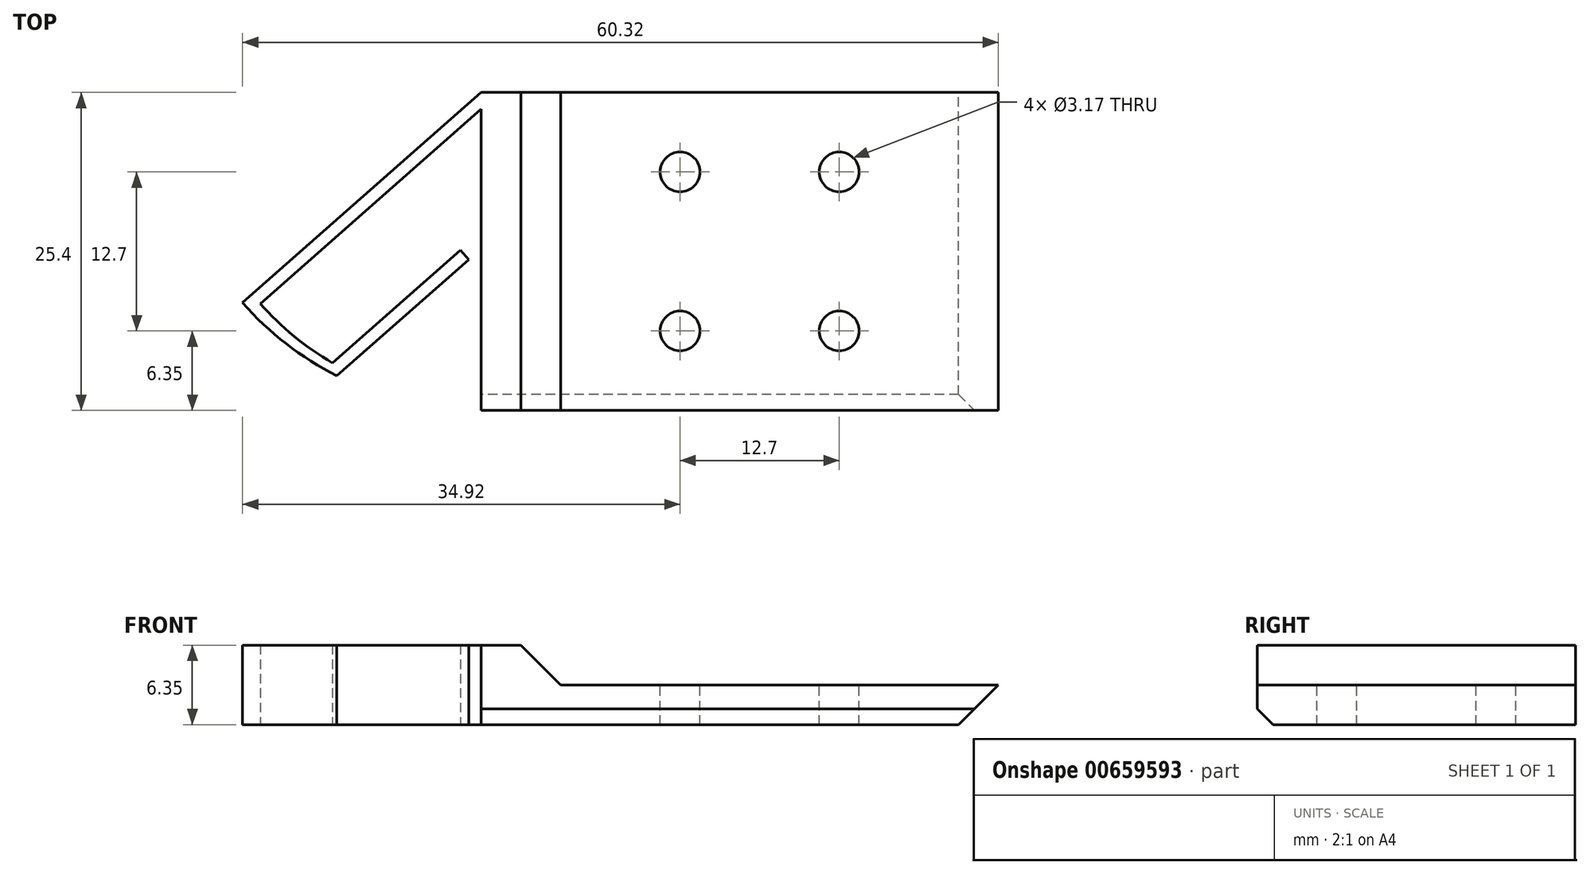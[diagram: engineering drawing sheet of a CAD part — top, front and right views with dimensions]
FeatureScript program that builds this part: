
annotation { "Feature Type Name" : "Feature", "Feature Type Description" : "" }
export const myFeature = defineFeature(function(context is Context, id is Id, definition is map)
    precondition{}
    {
        {
            var Q0;
            Q0=qCreatedBy(makeId("Top.planeOp"),FACE);
            var sketch = newSketch(context, id + "F0", { "sketchPlane" : qUnion([Q0])});
            skLineSegment(sketch, "E0.bottom", {"start": v(28.58, -12.7) * mm, "end": v(-28.58, -12.7) * mm});
            skLineSegment(sketch, "E0.top", {"start": v(28.58, 12.7) * mm, "end": v(-28.58, 12.7) * mm});
            skLineSegment(sketch, "E0.left", {"start": v(28.58, -12.7) * mm, "end": v(28.58, 12.7) * mm});
            skLineSegment(sketch, "E0.right", {"start": v(-28.57, -12.7) * mm, "end": v(-28.57, 12.7) * mm});
            skPoint(sketch, "E0.middle", {"position": v(0, 0) * mm});
            skLineSegment(sketch, "E1", {"start": v(-9.53, 11.37) * mm, "end": v(-9.52, -12.7) * mm});
            skLineSegment(sketch, "E2", {"start": v(0, -12.7) * mm, "end": v(0, 12.7) * mm});
            skPoint(sketch, "E3", {"position": v(-22.22, -12.7) * mm});
            skLineSegment(sketch, "E4", {"start": v(-9.53, 12.7) * mm, "end": v(-28.57, -4.1) * mm});
            skPoint(sketch, "E5", {"position": v(-19.05, -12.7) * mm});
            skArc(sketch, "E6", {"start": v(-28.57, -4.1) * mm, "mid": v(-25.09, -7.37) * mm, "end": v(-21.05, -9.94) * mm});
            skLineSegment(sketch, "E7", {"start": v(-21.05, -9.94) * mm, "end": v(-10.53, -0.66) * mm});
            skLineSegment(sketch, "E8", {"start": v(-10.53, -0.66) * mm, "end": v(-11.19, 0.1) * mm});
            skLineSegment(sketch, "E9", {"start": v(-11.19, 0.1) * mm, "end": v(-11.19, 0.1) * mm});
            skLineSegment(sketch, "E10", {"start": v(-9.53, 11.37) * mm, "end": v(-27.15, -4.18) * mm});
            skArc(sketch, "E11", {"start": v(-27.15, -4.18) * mm, "mid": v(-24.46, -6.77) * mm, "end": v(-21.4, -8.91) * mm});
            skLineSegment(sketch, "E12", {"start": v(-21.4, -8.91) * mm, "end": v(-11.19, 0.1) * mm});
            skSolve(sketch);
        }
        {
            var Q0;
            {var subQ0=sQuery(id+"F0.wireOp",EDGE,"E0.left");Q0=makeQuery(id+"F0.imprint","IMPRINT",FACE,{"disambiguationData":[TD([[makeQuery(id+"F0.imprint","IMPRINT",EDGE,{"derivedFrom":subQ0}),1.0]])]});}
            var Q1;
            {var subQ1=sQuery(id+"F0.wireOp",EDGE,"E1");Q1=makeQuery(id+"F0.imprint","IMPRINT",FACE,{"disambiguationData":[TD([[makeQuery(id+"F0.imprint","IMPRINT",EDGE,{"derivedFrom":subQ1}),1.0]])]});}
            var Q2;
            {var subQ0=sQuery(id+"F0.wireOp",EDGE,"Ll8NUgnO-918t-zldm-zNWz-RsUZQomu35K8");Q2=makeQuery(id+"F0.imprint","IMPRINT",FACE,{"disambiguationData":[TD([[makeQuery(id+"F0.imprint","IMPRINT",EDGE,{"derivedFrom":subQ0}),1.0]])]});}
            extrude(context, id + "F1", {"entities" : qUnion([Q0, Q1, Q2]), "depth" : 3.17 * mm, "offsetDistance" : 25.4 * mm});
        }
        {
            var Q0;
            {var subQ1=sQuery(id+"F0.wireOp",EDGE,"E1");Q0=makeQuery(id+"F0.imprint","IMPRINT",FACE,{"disambiguationData":[TD([[makeQuery(id+"F0.imprint","IMPRINT",EDGE,{"derivedFrom":subQ1}),1.0]])]});}
            extrude(context, id + "F2", {"entities" : qUnion([Q0]), "operationType" : NewBodyOperationType.ADD, "depth" : 6.35 * mm, "offsetDistance" : 25.4 * mm});
        }
        {
            var Q0;
            Q0=makeQuery(id+"F2.opExtrude","CAP_EDGE",EDGE,{"disambiguationData":[OSD([sQuery(id+"F0.wireOp",EDGE,"E2")])],"isStart":false});
            chamfer(context, id + "F3", {"entities" : qUnion([Q0]), "width" : 6.35 * mm, "tangentPropagation" : true});
        }
        {
            var Q0;
            {var subQ0=sQuery(id+"F0.wireOp",EDGE,"E0.left");Q0=makeQuery(id+"F37SAEC6IVc2ddh_1.boolean.opBoolean","MERGE",FACE,{"derivedFrom":[makeQuery(id+"F1.opExtrude","SWEPT_FACE",FACE,{"disambiguationData":[OSD([subQ0])]}),makeQuery(id+"F37SAEC6IVc2ddh_1.opExtrude","SWEPT_FACE",FACE,{"disambiguationData":[OSD([subQ0])]})]});}
            cPlane(context, id + "F4", {"entities" : qUnion([Q0]), "cplaneType" : CPlaneType.OFFSET, "offset" : 3.17 * mm, "width" : 152.4 * mm, "height" : 152.4 * mm});
        }
        {
            var Q0;
            {var subQ0=sQuery(id+"F0.wireOp",EDGE,"E1");Q0=makeQuery(id+"F2.boolean.opBoolean","MERGE",FACE,{"derivedFrom":[makeQuery(id+"F1.opExtrude","SWEPT_FACE",FACE,{"disambiguationData":[OSD([subQ0])]}),makeQuery(id+"F2.opExtrude","SWEPT_FACE",FACE,{"disambiguationData":[OSD([subQ0])]})]});}
            var sketch = newSketch(context, id + "F5", { "sketchPlane" : qUnion([Q0])});
            skLineSegment(sketch, "E13", {"start": v(12.7, 0) * mm, "end": v(12.7, 1.27) * mm});
            skLineSegment(sketch, "E14", {"start": v(12.7, 1.27) * mm, "end": v(11.43, 0) * mm});
            skLineSegment(sketch, "E15", {"start": v(11.43, 0) * mm, "end": v(12.7, 0) * mm});
            skSolve(sketch);
        }
        {
            var Q0;
            {var subQ0=sQuery(id+"F0.wireOp",EDGE,"E0.top");Q0=makeQuery(id+"F2.boolean.opBoolean","MERGE",FACE,{"derivedFrom":[makeQuery(id+"F1.opExtrude","SWEPT_FACE",FACE,{"disambiguationData":[OSD([subQ0])]}),makeQuery(id+"F2.opExtrude","SWEPT_FACE",FACE,{"disambiguationData":[OSD([subQ0])]})]});}
            var sketch = newSketch(context, id + "F6", { "sketchPlane" : qUnion([Q0])});
            skLineSegment(sketch, "E16", {"start": v(-28.58, 3.18) * mm, "end": v(-31.75, 3.18) * mm});
            skLineSegment(sketch, "E17", {"start": v(-31.75, 3.18) * mm, "end": v(-28.58, 0) * mm});
            skLineSegment(sketch, "E18", {"start": v(-28.58, 0) * mm, "end": v(-28.58, 3.18) * mm});
            skSolve(sketch);
        }
        {
            var Q0;
            Q0=makeQuery(id+"F6.imprint","IMPRINT",FACE,{"disambiguationData":[TD([[makeQuery(id+"F6.imprint","IMPRINT",EDGE,{"derivedFrom":sQuery(id+"F6.wireOp",EDGE,"E18")}),1.0]])]});
            var Q1;
            Q1=makeQuery(id+"F6.imprint","IMPRINT",FACE,{"disambiguationData":[TD([[makeQuery(id+"F6.imprint","IMPRINT",EDGE,{"derivedFrom":sQuery(id+"F6.wireOp",EDGE,"E16")}),1.0]])]});
            extrude(context, id + "F7", {"entities" : qUnion([Q0, Q1]), "operationType" : NewBodyOperationType.ADD, "oppositeDirection" : true, "depth" : 25.4 * mm, "offsetDistance" : 25.4 * mm});
        }
        {
            var Q0;
            Q0=makeQuery(id+"F5.imprint","IMPRINT",FACE,{"disambiguationData":[TD([[makeQuery(id+"F5.imprint","IMPRINT",EDGE,{"derivedFrom":sQuery(id+"F5.wireOp",EDGE,"E13")}),-1.0]])]});
            extrude(context, id + "F8", {"entities" : qUnion([Q0]), "operationType" : NewBodyOperationType.REMOVE, "oppositeDirection" : true, "depth" : 50.8 * mm, "offsetDistance" : 25.4 * mm});
        }
        {
            var Q0;
            Q0=makeQuery(id+"F1.opExtrude","SWEPT_BODY",BODY,{"disambiguationData":[OSD([sQuery(id+"F0.wireOp",EDGE,"E0.bottom"),sQuery(id+"F0.wireOp",EDGE,"E0.top"),sQuery(id+"F0.wireOp",EDGE,"E0.left"),sQuery(id+"F0.wireOp",EDGE,"E1"),sQuery(id+"F0.wireOp",EDGE,"E4"),sQuery(id+"F0.wireOp",EDGE,"E6"),sQuery(id+"F0.wireOp",EDGE,"E7"),sQuery(id+"F0.wireOp",EDGE,"E8"),sQuery(id+"F0.wireOp",EDGE,"E10"),sQuery(id+"F0.wireOp",EDGE,"E11"),sQuery(id+"F0.wireOp",EDGE,"E12")])]});
            var Q1;
            Q1=qCreatedBy(id+"F4.planeOp",FACE);
            mirror(context, id + "F9", {"entities" : qUnion([Q0]), "mirrorPlane" : qUnion([Q1])});
        }
        {
            var Q0;
            {var subQ0=sQuery(id+"F0.wireOp",EDGE,"E0.top");Q0=makeQuery(id+"F7.boolean.opBoolean","MERGE",FACE,{"derivedFrom":[makeQuery(id+"F1.opExtrude","CAP_FACE",FACE,{"disambiguationData":[OSD([sQuery(id+"F0.wireOp",EDGE,"E0.bottom"),subQ0,sQuery(id+"F0.wireOp",EDGE,"E0.left"),sQuery(id+"F0.wireOp",EDGE,"E1"),sQuery(id+"F0.wireOp",EDGE,"E4"),sQuery(id+"F0.wireOp",EDGE,"E6"),sQuery(id+"F0.wireOp",EDGE,"E7"),sQuery(id+"F0.wireOp",EDGE,"E8"),sQuery(id+"F0.wireOp",EDGE,"E10"),sQuery(id+"F0.wireOp",EDGE,"E11"),sQuery(id+"F0.wireOp",EDGE,"E12")])],"isStart":false}),makeQuery(id+"F7.opExtrude","SWEPT_FACE",FACE,{"disambiguationData":[OSD([subQ0,sQuery(id+"F6.wireOp",EDGE,"E16")])]})]});}
            var sketch = newSketch(context, id + "F10", { "sketchPlane" : qUnion([Q0])});
            skLineSegment(sketch, "E19", {"start": v(31.75, 0) * mm, "end": v(19.05, 0) * mm, "construction": true});
            skPoint(sketch, "E19.endSnap0", {"position": v(-3.17, 0) * mm});
            skLineSegment(sketch, "E20", {"start": v(19.05, 0) * mm, "end": v(6.35, 0) * mm, "construction": true});
            skLineSegment(sketch, "E21", {"start": v(6.35, 0) * mm, "end": v(6.35, 0) * mm});
            skLineSegment(sketch, "E22", {"start": v(31.75, 0) * mm, "end": v(44.45, 0) * mm, "construction": true});
            skLineSegment(sketch, "E23", {"start": v(44.45, 0) * mm, "end": v(57.15, 0) * mm, "construction": true});
            skLineSegment(sketch, "E24.bottom", {"start": v(44.45, 6.35) * mm, "end": v(19.05, 6.35) * mm, "construction": true});
            skLineSegment(sketch, "E24.top", {"start": v(44.45, -6.35) * mm, "end": v(19.05, -6.35) * mm, "construction": true});
            skLineSegment(sketch, "E24.left", {"start": v(44.45, 6.35) * mm, "end": v(44.45, -6.35) * mm, "construction": true});
            skLineSegment(sketch, "E24.right", {"start": v(19.05, 6.35) * mm, "end": v(19.05, -6.35) * mm, "construction": true});
            skPoint(sketch, "E24.middle", {"position": v(31.75, 0) * mm});
            skLineSegment(sketch, "E25.bottom", {"start": v(57.15, 6.35) * mm, "end": v(6.35, 6.35) * mm, "construction": true});
            skLineSegment(sketch, "E25.top", {"start": v(57.15, -6.35) * mm, "end": v(6.35, -6.35) * mm, "construction": true});
            skLineSegment(sketch, "E25.left", {"start": v(57.15, 6.35) * mm, "end": v(57.15, -6.35) * mm, "construction": true});
            skLineSegment(sketch, "E25.right", {"start": v(6.35, 6.35) * mm, "end": v(6.35, -6.35) * mm, "construction": true});
            skSolve(sketch);
        }
        {
            var Q0;
            Q0=sQuery(id+"F10.wireOp",VERTEX,"E25.left.end");
            var Q1;
            Q1=sQuery(id+"F10.wireOp",VERTEX,"E25.bottom.start");
            var Q2;
            Q2=sQuery(id+"F10.wireOp",VERTEX,"E24.bottom.end");
            var Q3;
            Q3=sQuery(id+"F10.wireOp",VERTEX,"E24.right.end");
            var Q4;
            Q4=sQuery(id+"F10.wireOp",VERTEX,"E25.right.end");
            var Q5;
            Q5=sQuery(id+"F10.wireOp",VERTEX,"E25.bottom.end");
            var Q6;
            Q6=sQuery(id+"F10.wireOp",VERTEX,"E24.top.start");
            var Q7;
            Q7=sQuery(id+"F10.wireOp",VERTEX,"E24.bottom.start");
            var Q8;
            Q8=makeQuery(id+"F1.opExtrude","SWEPT_BODY",BODY,{"disambiguationData":[OSD([sQuery(id+"F0.wireOp",EDGE,"E0.bottom"),sQuery(id+"F0.wireOp",EDGE,"E0.top"),sQuery(id+"F0.wireOp",EDGE,"E0.left"),sQuery(id+"F0.wireOp",EDGE,"E1"),sQuery(id+"F0.wireOp",EDGE,"E4"),sQuery(id+"F0.wireOp",EDGE,"E6"),sQuery(id+"F0.wireOp",EDGE,"E7"),sQuery(id+"F0.wireOp",EDGE,"E8"),sQuery(id+"F0.wireOp",EDGE,"E10"),sQuery(id+"F0.wireOp",EDGE,"E11"),sQuery(id+"F0.wireOp",EDGE,"E12")])]});
            var Q9;
            Q9=makeQuery(id+"F9.opPattern","COPY",BODY,{"derivedFrom":makeQuery(id+"F1.opExtrude","SWEPT_BODY",BODY,{"disambiguationData":[OSD([sQuery(id+"F0.wireOp",EDGE,"E0.bottom"),sQuery(id+"F0.wireOp",EDGE,"E0.top"),sQuery(id+"F0.wireOp",EDGE,"E0.left"),sQuery(id+"F0.wireOp",EDGE,"E1"),sQuery(id+"F0.wireOp",EDGE,"E4"),sQuery(id+"F0.wireOp",EDGE,"E6"),sQuery(id+"F0.wireOp",EDGE,"E7"),sQuery(id+"F0.wireOp",EDGE,"E8"),sQuery(id+"F0.wireOp",EDGE,"E10"),sQuery(id+"F0.wireOp",EDGE,"E11"),sQuery(id+"F0.wireOp",EDGE,"E12")])]}),"instanceName":"1"});
            hole(context, id + "F11", {"style" : HoleStyle.SIMPLE, "endStyle" : HoleEndStyle.THROUGH, "holeDiameter" : 3.17 * mm, "majorDiameter" : 6.35 * mm, "isTappedThrough" : true, "tappedDepth" : 12.7 * mm, "tapClearance" : 3, "locations" : qUnion([Q0, Q1, Q2, Q3, Q4, Q5, Q6, Q7]), "scope" : qUnion([Q8, Q9])});
        }
        {
            var Q0;
            Q0=makeQuery(id+"F9.opPattern","COPY",BODY,{"derivedFrom":makeQuery(id+"F1.opExtrude","SWEPT_BODY",BODY,{"disambiguationData":[OSD([sQuery(id+"F0.wireOp",EDGE,"E0.bottom"),sQuery(id+"F0.wireOp",EDGE,"E0.top"),sQuery(id+"F0.wireOp",EDGE,"E0.left"),sQuery(id+"F0.wireOp",EDGE,"E1"),sQuery(id+"F0.wireOp",EDGE,"E4"),sQuery(id+"F0.wireOp",EDGE,"E6"),sQuery(id+"F0.wireOp",EDGE,"E7"),sQuery(id+"F0.wireOp",EDGE,"E8"),sQuery(id+"F0.wireOp",EDGE,"E10"),sQuery(id+"F0.wireOp",EDGE,"E11"),sQuery(id+"F0.wireOp",EDGE,"E12")])]}),"instanceName":"1"});
            deleteBodies(context, id + "F12", {"entities" : qUnion([Q0])});
        }
    });
